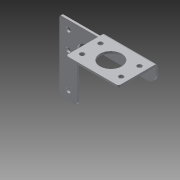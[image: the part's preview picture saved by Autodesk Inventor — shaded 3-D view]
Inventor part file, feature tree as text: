
AUTODESK INVENTOR PART (.ipt)
format: ipt  version: 2013 (Build 170138000, 138)  size: 228,352 bytes
history: native  units: in
note: dims shown in document units (in); Inventor stores cm internally (conversion verified against a paired STEP export)
features: sheet_metal_op x4, other x4, sketch x3, chamfer x1
ambient origin geometry x8: Origin, YZ Plane, XZ Plane, XY Plane, X Axis, Y Axis, Z Axis, Center Point
bodies: Solid1 (feature_tree)
feature tree (12):
  sheet_metal_op  "Face1"
  sheet_metal_op  "Flange1"
  chamfer  "Corner Round1"
  sketch  "Sketch1"  dims[d0=1.0in]
  other  "Plate1"
  sketch  "Sketch2"  dims[d2=0.26in]
  other  "Plate2"
  sheet_metal_op  "Bend1"
  sheet_metal_op  "Corner1"
  sketch  "Sketch3"  dims[d3=0.26in d4=2.0in d5=1.0in d6=4.5in d7=0.75in d8=3.0in d9=0.125in d10=0.12in d11=0.12in d12=0.06in d13=0.24in d14=0.12in d15=2.25in d16=90.0deg d17=0.05in d18=0.48in d19=0.12in d20=0.12in d21=0.5in d22=0.125in d23=0.26in d25=0.375in d26=0.5in d27=0.12in d28=0.0in d29=0.53in d30=0.395in d31=1.25in d32=2.0in d33=0.26in d34=0.5in d1=0.0625in]
  other  "Cut1"
  other  "Definition1"
